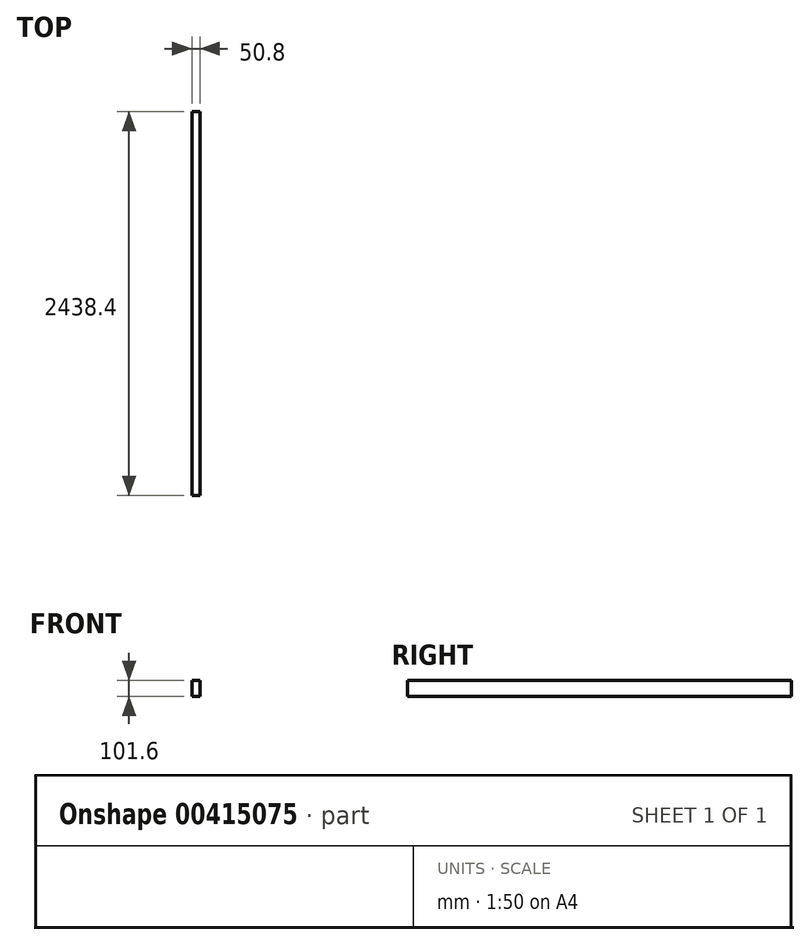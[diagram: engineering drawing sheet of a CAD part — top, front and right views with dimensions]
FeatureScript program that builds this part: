
annotation { "Feature Type Name" : "Feature", "Feature Type Description" : "" }
export const myFeature = defineFeature(function(context is Context, id is Id, definition is map)
    precondition{}
    {
        {
            var Q0;
            Q0=qCreatedBy(makeId("Front.planeOp"),FACE);
            var sketch = newSketch(context, id + "F0", { "sketchPlane" : qUnion([Q0])});
            skLineSegment(sketch, "E0.bottom", {"start": v(-25.4, -50.8) * mm, "end": v(25.4, -50.8) * mm});
            skLineSegment(sketch, "E0.top", {"start": v(-25.4, 50.8) * mm, "end": v(25.4, 50.8) * mm});
            skLineSegment(sketch, "E0.left", {"start": v(-25.4, -50.8) * mm, "end": v(-25.4, 50.8) * mm});
            skLineSegment(sketch, "E0.right", {"start": v(25.4, -50.8) * mm, "end": v(25.4, 50.8) * mm});
            skPoint(sketch, "E0.middle", {"position": v(0, 0) * mm});
            skSolve(sketch);
        }
        {
            var Q0;
            Q0 = qSketchRegion(id + "F0", true);
            extrude(context, id + "F1", {"entities" : qUnion([Q0]), "endBound" : BoundingType.SYMMETRIC, "depth" : 2438.4 * mm});
        }
    });
